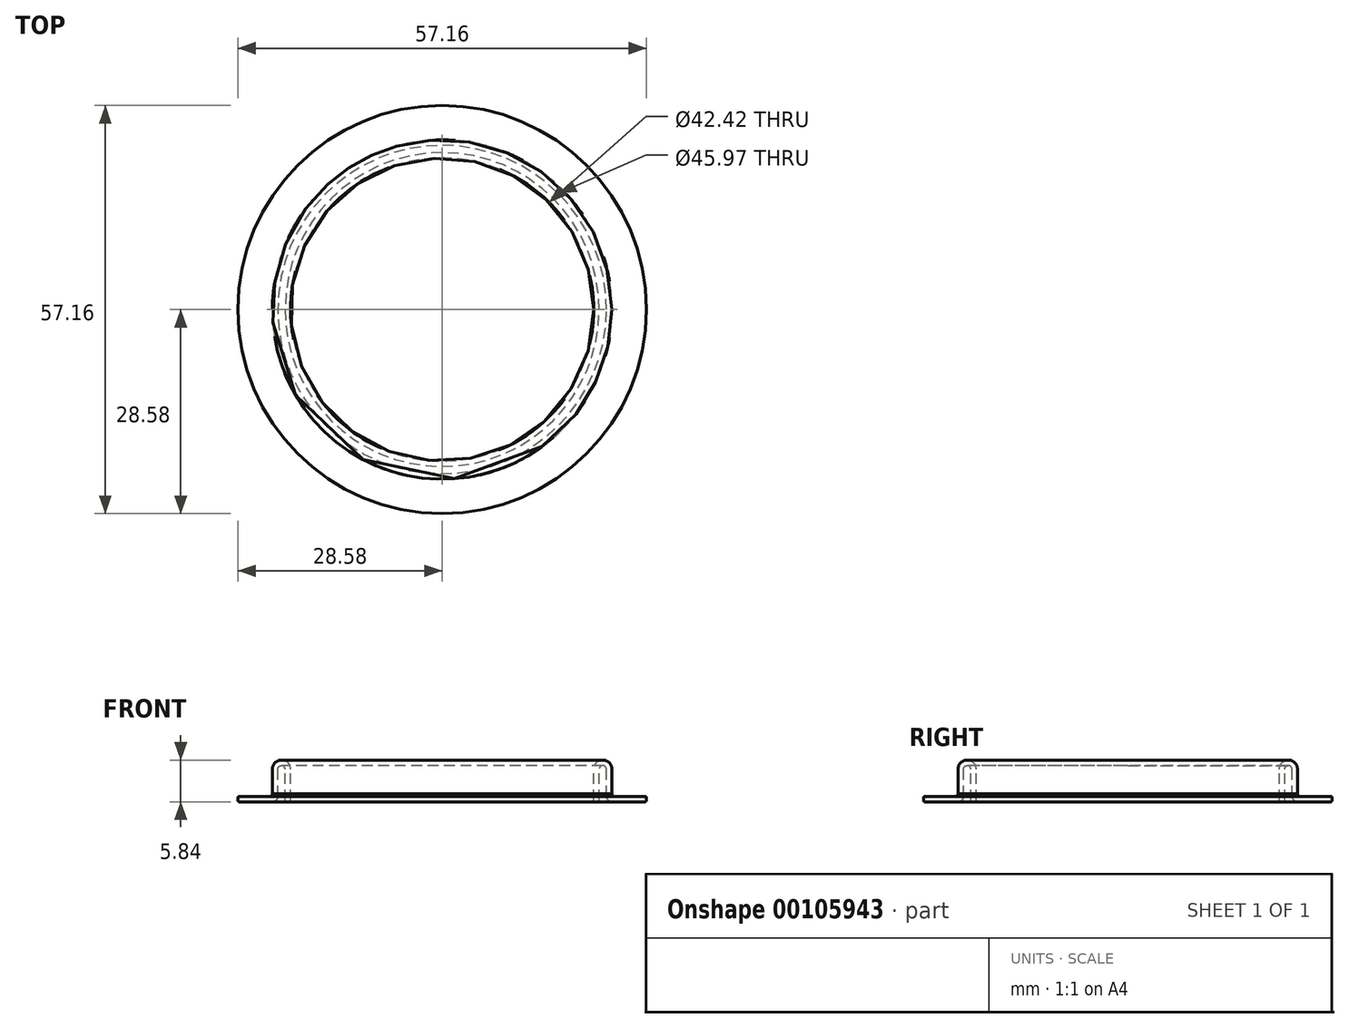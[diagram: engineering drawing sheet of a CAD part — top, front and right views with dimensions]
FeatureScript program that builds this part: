
annotation { "Feature Type Name" : "Feature", "Feature Type Description" : "" }
export const myFeature = defineFeature(function(context is Context, id is Id, definition is map)
    precondition{}
    {
        {
            var Q0;
            Q0=qCreatedBy(makeId("Front.planeOp"),FACE);
            var sketch = newSketch(context, id + "F0", { "sketchPlane" : qUnion([Q0])});
            skLineSegment(sketch, "E0", {"start": v(0, 19.5) * mm, "end": v(0, -22.59) * mm});
            skPoint(sketch, "E1.first.point", {"position": v(21.2, 4.73) * mm});
            skPoint(sketch, "E1.second.point", {"position": v(22.48, 5.84) * mm});
            skPoint(sketch, "E1.third.point", {"position": v(23.75, 4.65) * mm});
            skArc(sketch, "E2", {"start": v(23.75, 4.57) * mm, "mid": v(22.48, 5.84) * mm, "end": v(21.2, 4.57) * mm});
            skLineSegment(sketch, "E3", {"start": v(21.2, 4.57) * mm, "end": v(21.2, 0) * mm});
            skLineSegment(sketch, "E4", {"start": v(21.2, 0) * mm, "end": v(21.97, 0) * mm});
            skLineSegment(sketch, "E5", {"start": v(21.97, 0) * mm, "end": v(21.97, 4.57) * mm});
            skLineSegment(sketch, "E6", {"start": v(23.75, 0) * mm, "end": v(28.58, 0) * mm});
            skLineSegment(sketch, "E7", {"start": v(28.58, 0) * mm, "end": v(28.58, 0.76) * mm});
            skArc(sketch, "E8", {"start": v(22.99, 4.57) * mm, "mid": v(22.48, 5.07) * mm, "end": v(21.97, 4.57) * mm});
            skArc(sketch, "E9", {"start": v(22.99, 0.76) * mm, "mid": v(23.21, 0.22) * mm, "end": v(23.75, 0) * mm});
            skLineSegment(sketch, "E10", {"start": v(22.99, 0.76) * mm, "end": v(22.99, 1.14) * mm});
            skLineSegment(sketch, "E11", {"start": v(23.75, 0) * mm, "end": v(24.13, 0) * mm});
            skArc(sketch, "E12", {"start": v(23.75, 1.14) * mm, "mid": v(23.86, 0.87) * mm, "end": v(24.13, 0.76) * mm});
            skLineSegment(sketch, "E13", {"start": v(24.13, 0.76) * mm, "end": v(28.58, 0.76) * mm});
            skLineSegment(sketch, "E14", {"start": v(23.75, 1.14) * mm, "end": v(23.75, 4.65) * mm});
            skLineSegment(sketch, "E15", {"start": v(22.99, 0.76) * mm, "end": v(22.99, 4.57) * mm});
            skLineSegment(sketch, "E16", {"start": v(28.58, 0.76) * mm, "end": v(28.58, 0) * mm});
            skLineSegment(sketch, "E17", {"start": v(21.97, 4.57) * mm, "end": v(21.97, 0) * mm});
            skSolve(sketch);
        }
        {
            var Q0;
            {var subQ5=sQuery(id+"F0.wireOp",EDGE,"E3");Q0=makeQuery(id+"F0.imprint","IMPRINT",FACE,{"disambiguationData":[TD([[makeQuery(id+"F0.imprint","IMPRINT",EDGE,{"derivedFrom":subQ5}),1.0]])]});}
            var Q1;
            Q1=sQuery(id+"F0.wireOp",EDGE,"E0");
            revolve(context, id + "F1", {"entities" : qUnion([Q0]), "axis" : qUnion([Q1]), "revolveType" : RevolveType.FULL});
        }
        {
            var Q0;
            Q0=makeQuery(id+"F1.opRevolve","SWEPT_EDGE",EDGE,{"disambiguationData":[OSD([sQuery(id+"F0.wireOp",EDGE,"E6"),sQuery(id+"F0.wireOp",EDGE,"E16")])]});
            var Q1;
            Q1=makeQuery(id+"F1.opRevolve","SWEPT_EDGE",EDGE,{"disambiguationData":[OSD([sQuery(id+"F0.wireOp",EDGE,"E4"),sQuery(id+"F0.wireOp",EDGE,"E17")])]});
            var Q2;
            Q2=makeQuery(id+"F1.opRevolve","SWEPT_EDGE",EDGE,{"disambiguationData":[OSD([sQuery(id+"F0.wireOp",EDGE,"E3"),sQuery(id+"F0.wireOp",EDGE,"E4")])]});
            var Q3;
            Q3=makeQuery(id+"F1.opRevolve","SWEPT_EDGE",EDGE,{"disambiguationData":[OSD([sQuery(id+"F0.wireOp",EDGE,"E13"),sQuery(id+"F0.wireOp",EDGE,"E16")])]});
            fillet(context, id + "F2", {"entities" : qUnion([Q0, Q1, Q2, Q3]), "radius" : 0.2 * mm, "tangentPropagation" : true, "allowEdgeOverflow" : false});
        }
    });
